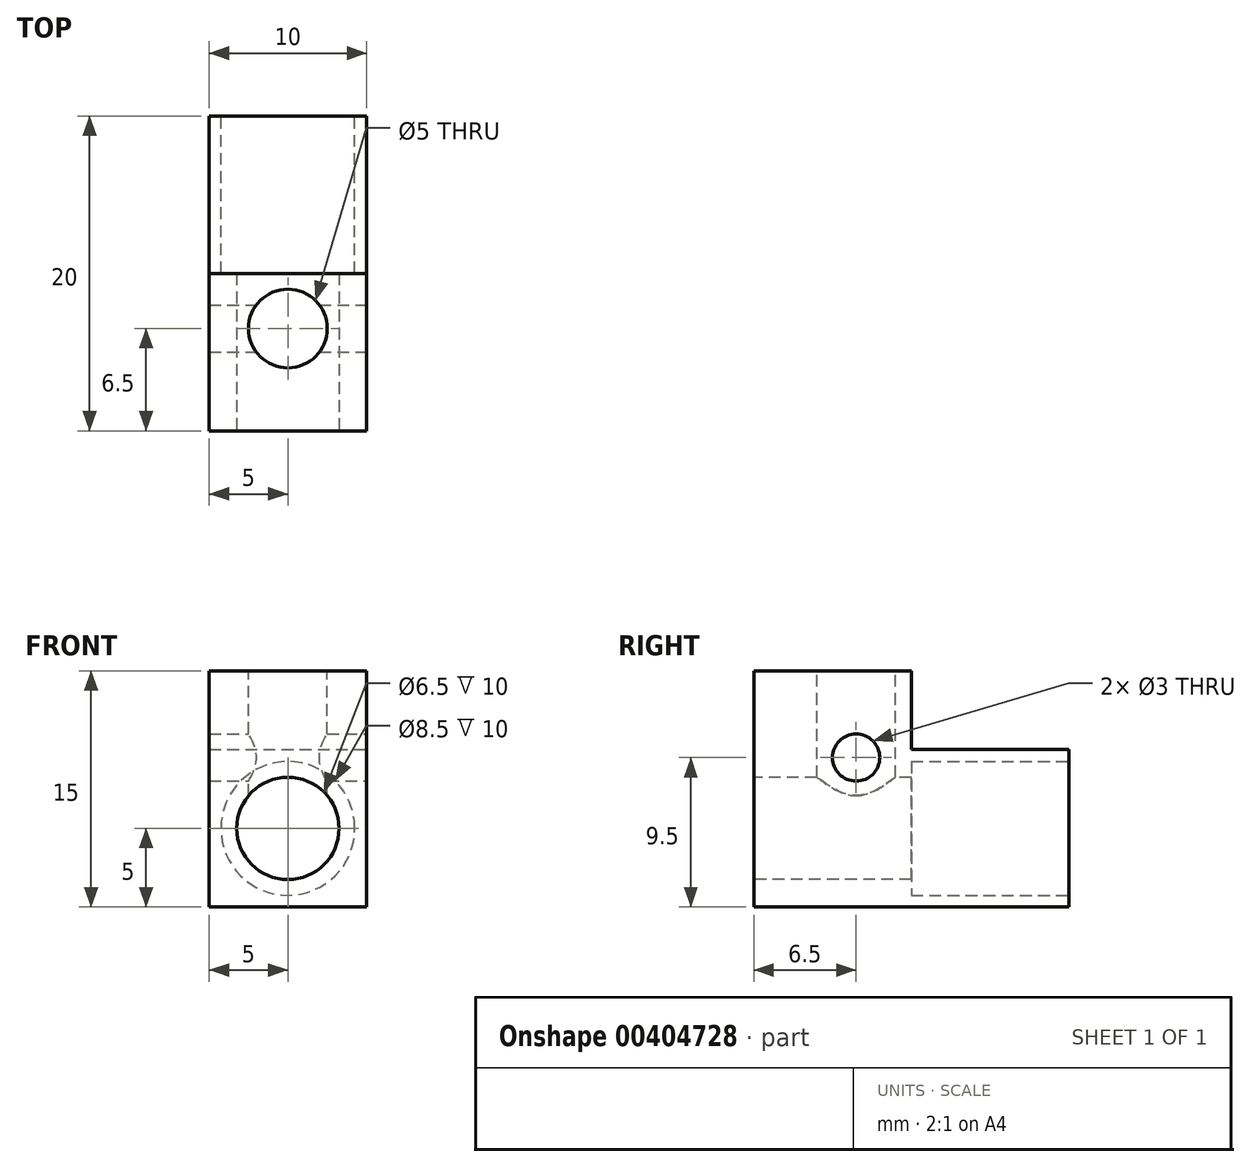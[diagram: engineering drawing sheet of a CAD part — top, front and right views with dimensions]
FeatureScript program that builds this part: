
annotation { "Feature Type Name" : "Feature", "Feature Type Description" : "" }
export const myFeature = defineFeature(function(context is Context, id is Id, definition is map)
    precondition{}
    {
        {
            var Q0;
            Q0=qCreatedBy(makeId("Front.planeOp"),FACE);
            var sketch = newSketch(context, id + "F0", { "sketchPlane" : qUnion([Q0])});
            skCircle(sketch, "E0", {"center": v(0, 0) * mm, "radius": 3.25 * mm});
            skLineSegment(sketch, "E1.bottom", {"start": v(5, -5) * mm, "end": v(-5, -5) * mm});
            skLineSegment(sketch, "E1.top", {"start": v(5, 10) * mm, "end": v(-5, 10) * mm});
            skLineSegment(sketch, "E1.left", {"start": v(5, -5) * mm, "end": v(5, 10) * mm});
            skLineSegment(sketch, "E1.right", {"start": v(-5, -5) * mm, "end": v(-5, 10) * mm});
            skPoint(sketch, "E1.middle", {"position": v(0, 2.5) * mm});
            skLineSegment(sketch, "E2", {"start": v(-5, 5) * mm, "end": v(5, 5) * mm});
            skPoint(sketch, "E2.endSnap0", {"position": v(5, 2.5) * mm});
            skSolve(sketch);
        }
        {
            var Q0;
            Q0=makeQuery(id+"F0.imprint","IMPRINT",FACE,{"disambiguationData":[TD([[makeQuery(id+"F0.imprint","IMPRINT",EDGE,{"derivedFrom":sQuery(id+"F0.wireOp",EDGE,"E0")}),-1.0]])]});
            extrude(context, id + "F1", {"entities" : qUnion([Q0]), "oppositeDirection" : true, "depth" : 10 * mm});
        }
        {
            var Q0;
            {var subQ0=sQuery(id+"F0.wireOp",EDGE,"E1.top");Q0=makeQuery(id+"F0.imprint","IMPRINT",FACE,{"disambiguationData":[TD([[makeQuery(id+"F0.imprint","IMPRINT",EDGE,{"derivedFrom":subQ0}),1.0]])]});}
            var Q1;
            Q1=makeQuery(id+"F0.imprint","IMPRINT",FACE,{"disambiguationData":[TD([[makeQuery(id+"F0.imprint","IMPRINT",EDGE,{"derivedFrom":sQuery(id+"F0.wireOp",EDGE,"E0")}),-1.0]])]});
            extrude(context, id + "F2", {"entities" : qUnion([Q0, Q1]), "operationType" : NewBodyOperationType.ADD, "depth" : 10 * mm});
        }
        {
            var Q0;
            Q0=makeQuery(id+"F1.opExtrude","CAP_FACE",FACE,{"disambiguationData":[OSD([sQuery(id+"F0.wireOp",EDGE,"E0"),sQuery(id+"F0.wireOp",EDGE,"E1.bottom"),sQuery(id+"F0.wireOp",EDGE,"E1.left"),sQuery(id+"F0.wireOp",EDGE,"E1.right"),sQuery(id+"F0.wireOp",EDGE,"E2")])],"isStart":false});
            var sketch = newSketch(context, id + "F3", { "sketchPlane" : qUnion([Q0])});
            skCircle(sketch, "E3", {"center": v(0, 0) * mm, "radius": 4.25 * mm});
            skSolve(sketch);
        }
        {
            var Q0;
            Q0=makeQuery(id+"F3.imprint","IMPRINT",FACE,{"disambiguationData":[TD([[makeQuery(id+"F3.imprint","IMPRINT",EDGE,{"derivedFrom":makeQuery(id+"F1.opExtrude","CAP_EDGE",EDGE,{"disambiguationData":[OSD([sQuery(id+"F0.wireOp",EDGE,"E0")])],"isStart":false})}),1.0]])]});
            extrude(context, id + "F4", {"entities" : qUnion([Q0]), "operationType" : NewBodyOperationType.REMOVE, "oppositeDirection" : true, "depth" : 10 * mm});
        }
        {
            var Q0;
            Q0=qCreatedBy(makeId("Right.planeOp"),FACE);
            var sketch = newSketch(context, id + "F5", { "sketchPlane" : qUnion([Q0])});
            skCircle(sketch, "E4", {"center": v(-3.5, 4.5) * mm, "radius": 1.5 * mm});
            skLineSegment(sketch, "E5", {"start": v(0, 3) * mm, "end": v(-10, 3) * mm, "construction": true});
            skSolve(sketch);
        }
        {
            var Q0;
            Q0=makeQuery(id+"F5.imprint","IMPRINT",FACE,{"disambiguationData":[TD([[makeQuery(id+"F5.imprint","IMPRINT",EDGE,{"derivedFrom":sQuery(id+"F5.wireOp",EDGE,"E4")}),1.0]])]});
            extrude(context, id + "F6", {"entities" : qUnion([Q0]), "operationType" : NewBodyOperationType.REMOVE, "endBound" : BoundingType.THROUGH_ALL, "oppositeDirection" : true, "depth" : 25 * mm, "hasSecondDirection" : true, "secondDirectionBound" : BoundingType.THROUGH_ALL, "secondDirectionOppositeDirection" : false, "secondDirectionDepth" : 25 * mm});
        }
        {
            var Q0;
            Q0=makeQuery(id+"F2.opExtrude","SWEPT_FACE",FACE,{"disambiguationData":[OSD([sQuery(id+"F0.wireOp",EDGE,"E1.top")])]});
            var sketch = newSketch(context, id + "F7", { "sketchPlane" : qUnion([Q0])});
            skCircle(sketch, "E6", {"center": v(0, -3.5) * mm, "radius": 2.5 * mm});
            skSolve(sketch);
        }
        {
            var Q0;
            Q0=makeQuery(id+"F7.imprint","IMPRINT",FACE,{"disambiguationData":[TD([[makeQuery(id+"F7.imprint","IMPRINT",EDGE,{"derivedFrom":sQuery(id+"F7.wireOp",EDGE,"E6")}),1.0]])]});
            extrude(context, id + "F8", {"entities" : qUnion([Q0]), "operationType" : NewBodyOperationType.REMOVE, "oppositeDirection" : true, "depth" : 10 * mm});
        }
    });
